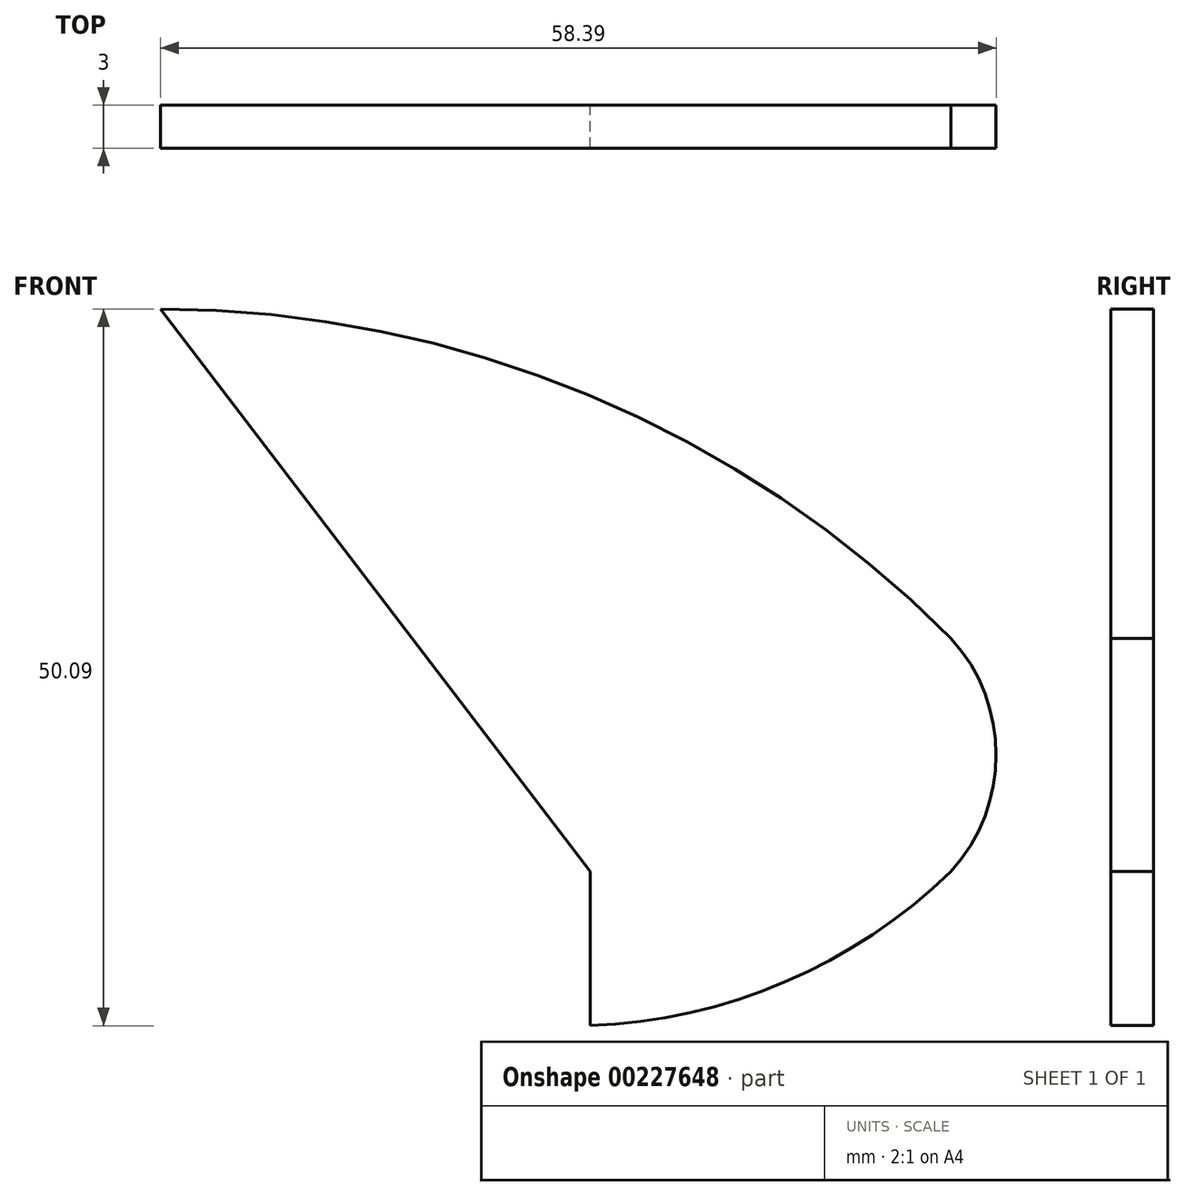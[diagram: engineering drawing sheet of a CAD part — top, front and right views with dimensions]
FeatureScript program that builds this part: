
annotation { "Feature Type Name" : "Feature", "Feature Type Description" : "" }
export const myFeature = defineFeature(function(context is Context, id is Id, definition is map)
    precondition{}
    {
        {
            var Q0;
            Q0=qCreatedBy(makeId("Front.planeOp"),FACE);
            var sketch = newSketch(context, id + "F0", { "sketchPlane" : qUnion([Q0])});
            skArc(sketch, "E0", {"start": v(55.24, 16.3) * mm, "mid": v(29.9, 33.3) * mm, "end": v(0, 39.3) * mm});
            skArc(sketch, "E1", {"start": v(55.24, 0) * mm, "mid": v(58.39, 8.15) * mm, "end": v(55.24, 16.3) * mm});
            skArc(sketch, "E2", {"start": v(30.01, -10.78) * mm, "mid": v(43.62, -7.73) * mm, "end": v(55.24, 0) * mm});
            skLineSegment(sketch, "E3", {"start": v(30.01, -10.78) * mm, "end": v(30.01, 0) * mm});
            skLineSegment(sketch, "E4", {"start": v(30.01, 0) * mm, "end": v(0, 39.3) * mm});
            skSolve(sketch);
        }
        {
            var Q0;
            Q0 = qSketchRegion(id + "F0", true);
            extrude(context, id + "F1", {"entities" : qUnion([Q0]), "depth" : 3 * mm});
        }
    });
